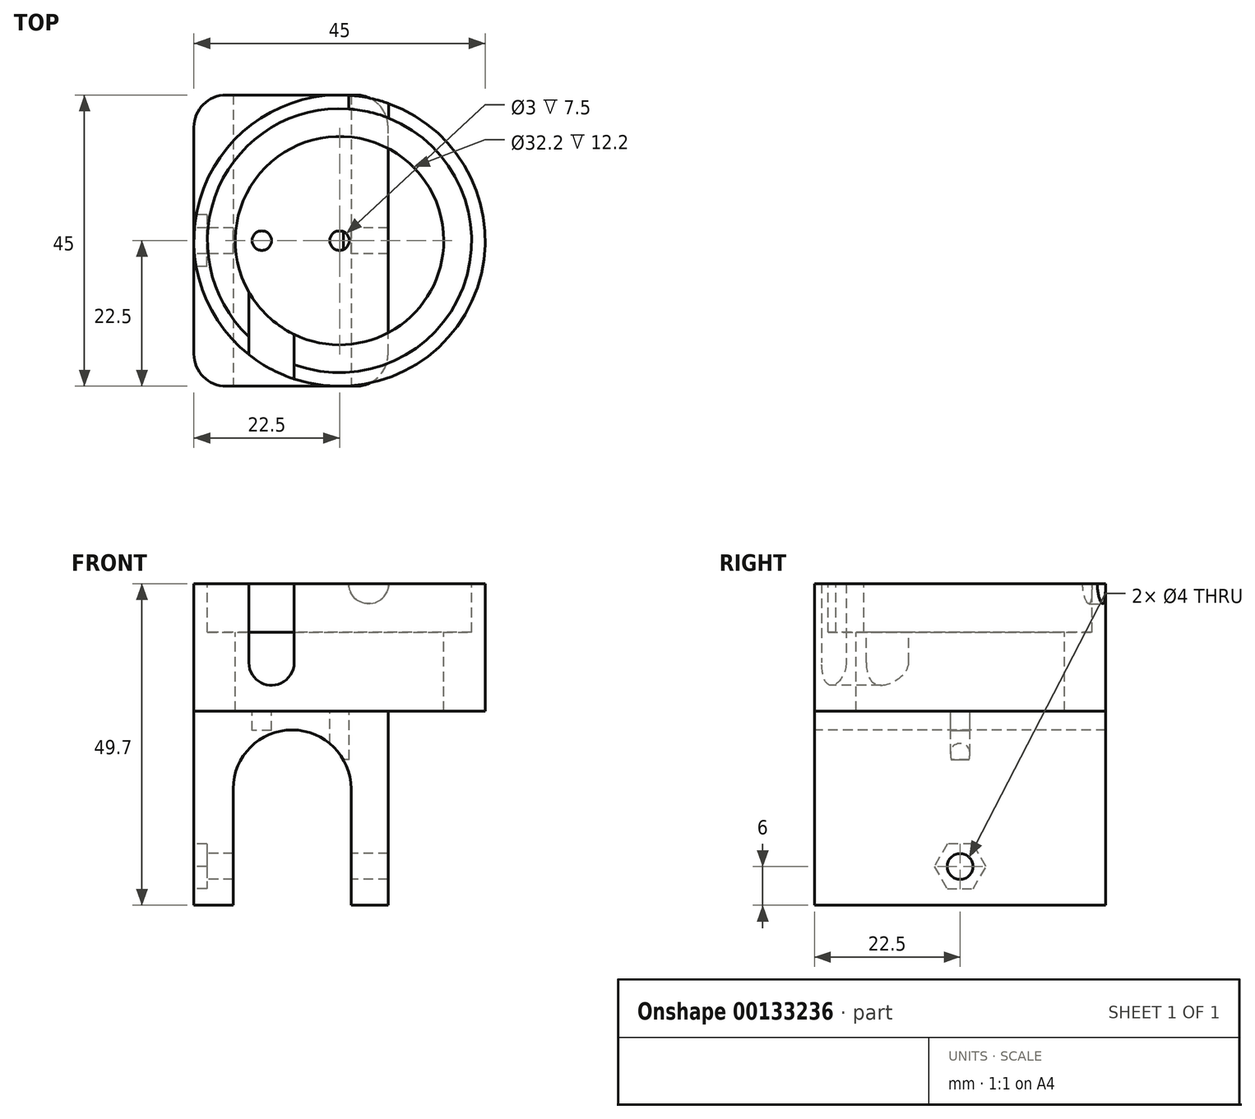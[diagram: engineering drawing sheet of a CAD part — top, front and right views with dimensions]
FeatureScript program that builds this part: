
annotation { "Feature Type Name" : "Feature", "Feature Type Description" : "" }
export const myFeature = defineFeature(function(context is Context, id is Id, definition is map)
    precondition{}
    {
        {
            var Q0;
            Q0=qCreatedBy(makeId("Top.planeOp"),FACE);
            var sketch = newSketch(context, id + "F0", { "sketchPlane" : qUnion([Q0])});
            skLineSegment(sketch, "E0.bottom", {"start": v(22.5, -22.5) * mm, "end": v(-22.5, -22.5) * mm});
            skLineSegment(sketch, "E0.top", {"start": v(22.5, 22.5) * mm, "end": v(-22.5, 22.5) * mm});
            skLineSegment(sketch, "E0.left", {"start": v(22.5, -22.5) * mm, "end": v(22.5, 22.5) * mm});
            skLineSegment(sketch, "E0.right", {"start": v(-22.5, -22.5) * mm, "end": v(-22.5, 22.5) * mm});
            skPoint(sketch, "E0.middle", {"position": v(0, 0) * mm});
            skSolve(sketch);
        }
        {
            var Q0;
            Q0 = qSketchRegion(id + "F0", true);
            extrude(context, id + "F1", {"entities" : qUnion([Q0]), "depth" : 19.7 * mm});
        }
        {
            var Q0;
            Q0=makeQuery(id+"F1.opExtrude","CAP_FACE",FACE,{"disambiguationData":[OSD([sQuery(id+"F0.wireOp",EDGE,"E0.bottom"),sQuery(id+"F0.wireOp",EDGE,"E0.top"),sQuery(id+"F0.wireOp",EDGE,"E0.left"),sQuery(id+"F0.wireOp",EDGE,"E0.right")])],"isStart":false});
            var sketch = newSketch(context, id + "F2", { "sketchPlane" : qUnion([Q0])});
            skCircle(sketch, "E1", {"center": v(0, 0) * mm, "radius": 20.4 * mm});
            skSolve(sketch);
        }
        {
            var Q0;
            Q0=makeQuery(id+"F2.imprint","IMPRINT",FACE,{"disambiguationData":[TD([[makeQuery(id+"F2.imprint","IMPRINT",EDGE,{"derivedFrom":sQuery(id+"F2.wireOp",EDGE,"E1")}),1.0]])]});
            extrude(context, id + "F3", {"entities" : qUnion([Q0]), "operationType" : NewBodyOperationType.REMOVE, "oppositeDirection" : true, "depth" : 7.5 * mm});
        }
        {
            var Q0;
            Q0=makeQuery(id+"F3.boolean.opBoolean","COPY",FACE,{"derivedFrom":makeQuery(id+"F3.opExtrude","CAP_FACE",FACE,{"disambiguationData":[OSD([sQuery(id+"F2.wireOp",EDGE,"E1")])],"isStart":false})});
            var sketch = newSketch(context, id + "F4", { "sketchPlane" : qUnion([Q0])});
            skCircle(sketch, "E2", {"center": v(0, 0) * mm, "radius": 16.1 * mm});
            skSolve(sketch);
        }
        {
            var Q0;
            Q0=makeQuery(id+"F4.imprint","IMPRINT",FACE,{"disambiguationData":[TD([[makeQuery(id+"F4.imprint","IMPRINT",EDGE,{"derivedFrom":sQuery(id+"F4.wireOp",EDGE,"E2")}),1.0]])]});
            extrude(context, id + "F5", {"entities" : qUnion([Q0]), "operationType" : NewBodyOperationType.REMOVE, "endBound" : BoundingType.UP_TO_NEXT, "oppositeDirection" : true, "depth" : 25 * mm});
        }
        {
            var Q0;
            Q0=makeQuery(id+"F1.opExtrude","SWEPT_FACE",FACE,{"disambiguationData":[OSD([sQuery(id+"F0.wireOp",EDGE,"E0.bottom")])]});
            var sketch = newSketch(context, id + "F6", { "sketchPlane" : qUnion([Q0])});
            skArc(sketch, "E3", {"start": v(-14, 7.5) * mm, "mid": v(-10.5, 4) * mm, "end": v(-7, 7.5) * mm});
            skLineSegment(sketch, "E4", {"start": v(-10.5, 7.5) * mm, "end": v(-22.5, 7.5) * mm, "construction": true});
            skLineSegment(sketch, "E5", {"start": v(-10.5, 7.5) * mm, "end": v(0, 7.5) * mm, "construction": true});
            skLineSegment(sketch, "E6", {"start": v(-7, 7.5) * mm, "end": v(-7, 19.7) * mm});
            skLineSegment(sketch, "E7", {"start": v(-14, 7.5) * mm, "end": v(-14, 19.7) * mm});
            skLineSegment(sketch, "E8", {"start": v(-7, 19.7) * mm, "end": v(-14, 19.7) * mm});
            skSolve(sketch);
        }
        {
            var Q0;
            Q0=makeQuery(id+"F6.imprint","IMPRINT",FACE,{"disambiguationData":[TD([[makeQuery(id+"F6.imprint","IMPRINT",EDGE,{"derivedFrom":sQuery(id+"F6.wireOp",EDGE,"E3")}),1.0]])]});
            extrude(context, id + "F7", {"entities" : qUnion([Q0]), "operationType" : NewBodyOperationType.REMOVE, "endBound" : BoundingType.UP_TO_NEXT, "oppositeDirection" : true, "depth" : 25 * mm});
        }
        {
            var Q0;
            Q0=makeQuery(id+"F1.opExtrude","SWEPT_FACE",FACE,{"disambiguationData":[OSD([sQuery(id+"F0.wireOp",EDGE,"E0.top")])]});
            var sketch = newSketch(context, id + "F8", { "sketchPlane" : qUnion([Q0])});
            skArc(sketch, "E9", {"start": v(-7.6, 19.7) * mm, "mid": v(-4.5, 16.6) * mm, "end": v(-1.4, 19.7) * mm});
            skLineSegment(sketch, "E10", {"start": v(-7.6, 19.7) * mm, "end": v(-1.4, 19.7) * mm});
            skSolve(sketch);
        }
        {
            var Q0;
            Q0=makeQuery(id+"F8.imprint","IMPRINT",FACE,{"disambiguationData":[TD([[makeQuery(id+"F8.imprint","IMPRINT",EDGE,{"derivedFrom":sQuery(id+"F8.wireOp",EDGE,"E9")}),1.0]])]});
            extrude(context, id + "F9", {"entities" : qUnion([Q0]), "operationType" : NewBodyOperationType.REMOVE, "endBound" : BoundingType.UP_TO_NEXT, "oppositeDirection" : true, "depth" : 25 * mm});
        }
        {
            var Q0;
            Q0=makeQuery(id+"F1.opExtrude","CAP_FACE",FACE,{"disambiguationData":[OSD([sQuery(id+"F0.wireOp",EDGE,"E0.bottom"),sQuery(id+"F0.wireOp",EDGE,"E0.top"),sQuery(id+"F0.wireOp",EDGE,"E0.left"),sQuery(id+"F0.wireOp",EDGE,"E0.right")])],"isStart":true});
            var sketch = newSketch(context, id + "F10", { "sketchPlane" : qUnion([Q0])});
            skLineSegment(sketch, "E11.bottom", {"start": v(-22.5, 22.5) * mm, "end": v(7.5, 22.5) * mm});
            skLineSegment(sketch, "E11.top", {"start": v(-22.5, -22.5) * mm, "end": v(7.5, -22.5) * mm});
            skLineSegment(sketch, "E11.left", {"start": v(-22.5, 22.5) * mm, "end": v(-22.5, -22.5) * mm});
            skLineSegment(sketch, "E11.right", {"start": v(7.5, 22.5) * mm, "end": v(7.5, -22.5) * mm});
            skSolve(sketch);
        }
        {
            var Q0;
            {var subQ1=sQuery(id+"F10.wireOp",EDGE,"E11.bottom");Q0=makeQuery(id+"F10.imprint","IMPRINT",FACE,{"disambiguationData":[TD([[makeQuery(id+"F10.imprint","IMPRINT",EDGE,{"derivedFrom":subQ1}),1.0]])]});}
            var Q1;
            {var subQ0=sQuery(id+"F10.wireOp",EDGE,"E11.right");var subQ1=makeQuery(id+"F5.boolean.opBoolean","COPY",EDGE,{"derivedFrom":makeQuery(id+"F5.opExtrude","TWEAK_EDGE",EDGE,{"derivedFrom":[makeQuery(id+"F1.opExtrude","CAP_FACE",FACE,{"disambiguationData":[OSD([sQuery(id+"F0.wireOp",EDGE,"E0.bottom"),sQuery(id+"F0.wireOp",EDGE,"E0.top"),sQuery(id+"F0.wireOp",EDGE,"E0.left"),sQuery(id+"F0.wireOp",EDGE,"E0.right")])],"isStart":true}),makeQuery(id+"F4.imprint","IMPRINT",EDGE,{"derivedFrom":sQuery(id+"F4.wireOp",EDGE,"E2")})]})});var subQ2=makeQuery(id+"F10.imprint","INTERSECT",VERTEX,{"disambiguationData":[OD(0.0)],"derivedFrom":[subQ1,subQ0]});Q1=makeQuery(id+"F10.imprint","IMPRINT",FACE,{"disambiguationData":[TD([[makeQuery(id+"F10.imprint","IMPRINT",EDGE,{"disambiguationData":[TD([[subQ2,-1.0]])],"derivedFrom":subQ0}),-1.0]])]});}
            extrude(context, id + "F11", {"entities" : qUnion([Q0, Q1]), "depth" : 30 * mm});
        }
        {
            var Q0;
            Q0=makeQuery(id+"F11.boolean.opBoolean","MERGE",FACE,{"derivedFrom":[makeQuery(id+"F1.opExtrude","SWEPT_FACE",FACE,{"disambiguationData":[OSD([sQuery(id+"F0.wireOp",EDGE,"E0.bottom")])]}),makeQuery(id+"F11.opExtrude","SWEPT_FACE",FACE,{"disambiguationData":[OSD([sQuery(id+"F10.wireOp",EDGE,"E11.bottom")])]})]});
            var sketch = newSketch(context, id + "F12", { "sketchPlane" : qUnion([Q0])});
            skLineSegment(sketch, "E12", {"start": v(-7.5, -30) * mm, "end": v(-7, 19.7) * mm, "construction": true});
            skArc(sketch, "E13", {"start": v(1.78, -12) * mm, "mid": v(-7.32, -2.9) * mm, "end": v(-16.42, -12) * mm});
            skLineSegment(sketch, "E14", {"start": v(-22.5, -12) * mm, "end": v(7.5, -12) * mm, "construction": true});
            skLineSegment(sketch, "E15", {"start": v(-16.42, -12) * mm, "end": v(-16.42, -30) * mm});
            skLineSegment(sketch, "E16", {"start": v(1.78, -12) * mm, "end": v(1.78, -30) * mm});
            skLineSegment(sketch, "E17", {"start": v(1.78, -30) * mm, "end": v(-16.42, -30) * mm});
            skSolve(sketch);
        }
        {
            var Q0;
            Q0=makeQuery(id+"F12.imprint","IMPRINT",FACE,{"disambiguationData":[TD([[makeQuery(id+"F12.imprint","IMPRINT",EDGE,{"derivedFrom":sQuery(id+"F12.wireOp",EDGE,"E13")}),1.0]])]});
            extrude(context, id + "F13", {"entities" : qUnion([Q0]), "operationType" : NewBodyOperationType.REMOVE, "endBound" : BoundingType.UP_TO_NEXT, "oppositeDirection" : true, "depth" : 25 * mm});
        }
        {
            var Q0;
            Q0=makeQuery(id+"F1.opExtrude","SWEPT_EDGE",EDGE,{"disambiguationData":[OSD([sQuery(id+"F0.wireOp",EDGE,"E0.bottom"),sQuery(id+"F0.wireOp",EDGE,"E0.left")])]});
            var Q1;
            Q1=makeQuery(id+"F1.opExtrude","SWEPT_EDGE",EDGE,{"disambiguationData":[OSD([sQuery(id+"F0.wireOp",EDGE,"E0.bottom"),sQuery(id+"F0.wireOp",EDGE,"E0.right")])]});
            var Q2;
            Q2=makeQuery(id+"F1.opExtrude","SWEPT_EDGE",EDGE,{"disambiguationData":[OSD([sQuery(id+"F0.wireOp",EDGE,"E0.top"),sQuery(id+"F0.wireOp",EDGE,"E0.right")])]});
            var Q3;
            Q3=makeQuery(id+"F1.opExtrude","SWEPT_EDGE",EDGE,{"disambiguationData":[OSD([sQuery(id+"F0.wireOp",EDGE,"E0.top"),sQuery(id+"F0.wireOp",EDGE,"E0.left")])]});
            fillet(context, id + "F14", {"entities" : qUnion([Q0, Q1, Q2, Q3]), "radius" : 22.5 * mm, "tangentPropagation" : true, "allowEdgeOverflow" : false});
        }
        {
            var Q0;
            Q0=makeQuery(id+"F11.opExtrude","SWEPT_FACE",FACE,{"disambiguationData":[OSD([sQuery(id+"F10.wireOp",EDGE,"E11.left")])]});
            var sketch = newSketch(context, id + "F15", { "sketchPlane" : qUnion([Q0])});
            skCircle(sketch, "E18.cCircle", {"center": v(0, -24) * mm, "radius": 4 * mm, "construction": true});
            skLineSegment(sketch, "E18.0", {"start": v(2, -27.46) * mm, "end": v(-2, -27.46) * mm});
            skLineSegment(sketch, "E18.1", {"start": v(-2, -27.46) * mm, "end": v(-4, -24) * mm});
            skLineSegment(sketch, "E18.2", {"start": v(-4, -24) * mm, "end": v(-2, -20.54) * mm});
            skLineSegment(sketch, "E18.3", {"start": v(-2, -20.54) * mm, "end": v(2, -20.54) * mm});
            skLineSegment(sketch, "E18.4", {"start": v(2, -20.54) * mm, "end": v(4, -24) * mm});
            skLineSegment(sketch, "E18.5", {"start": v(4, -24) * mm, "end": v(2, -27.46) * mm});
            skSolve(sketch);
        }
        {
            var Q0;
            Q0=makeQuery(id+"F15.imprint","IMPRINT",FACE,{"disambiguationData":[TD([[makeQuery(id+"F15.imprint","IMPRINT",EDGE,{"derivedFrom":sQuery(id+"F15.wireOp",EDGE,"E18.0")}),-1.0]])]});
            extrude(context, id + "F16", {"entities" : qUnion([Q0]), "operationType" : NewBodyOperationType.REMOVE, "oppositeDirection" : true, "depth" : 2 * mm});
        }
        {
            var Q0;
            Q0=makeQuery(id+"F16.boolean.opBoolean","COPY",FACE,{"derivedFrom":makeQuery(id+"F16.opExtrude","CAP_FACE",FACE,{"disambiguationData":[OSD([sQuery(id+"F15.wireOp",EDGE,"E18.0"),sQuery(id+"F15.wireOp",EDGE,"E18.1"),sQuery(id+"F15.wireOp",EDGE,"E18.2"),sQuery(id+"F15.wireOp",EDGE,"E18.3"),sQuery(id+"F15.wireOp",EDGE,"E18.4"),sQuery(id+"F15.wireOp",EDGE,"E18.5")])],"isStart":false})});
            var sketch = newSketch(context, id + "F17", { "sketchPlane" : qUnion([Q0])});
            skLineSegment(sketch, "E19", {"start": v(-4, -24) * mm, "end": v(4, -24) * mm, "construction": true});
            skCircle(sketch, "E20", {"center": v(0, -24) * mm, "radius": 2 * mm});
            skSolve(sketch);
        }
        {
            var Q0;
            Q0=makeQuery(id+"F17.imprint","IMPRINT",FACE,{"disambiguationData":[TD([[makeQuery(id+"F17.imprint","IMPRINT",EDGE,{"derivedFrom":sQuery(id+"F17.wireOp",EDGE,"E20")}),1.0]])]});
            extrude(context, id + "F18", {"entities" : qUnion([Q0]), "operationType" : NewBodyOperationType.REMOVE, "endBound" : BoundingType.THROUGH_ALL, "oppositeDirection" : true, "depth" : 25 * mm});
        }
        {
            var Q0;
            Q0=makeQuery(id+"F11.opExtrude","SWEPT_EDGE",EDGE,{"disambiguationData":[OSD([sQuery(id+"F10.wireOp",EDGE,"E11.bottom"),sQuery(id+"F10.wireOp",EDGE,"E11.left")])]});
            var Q1;
            Q1=makeQuery(id+"F11.opExtrude","SWEPT_EDGE",EDGE,{"disambiguationData":[OSD([sQuery(id+"F0.wireOp",EDGE,"E0.bottom"),sQuery(id+"F10.wireOp",EDGE,"E11.bottom"),sQuery(id+"F10.wireOp",EDGE,"E11.right")])]});
            var Q2;
            Q2=makeQuery(id+"F11.opExtrude","SWEPT_EDGE",EDGE,{"disambiguationData":[OSD([sQuery(id+"F0.wireOp",EDGE,"E0.top"),sQuery(id+"F10.wireOp",EDGE,"E11.top"),sQuery(id+"F10.wireOp",EDGE,"E11.right")])]});
            var Q3;
            Q3=makeQuery(id+"F11.opExtrude","SWEPT_EDGE",EDGE,{"disambiguationData":[OSD([sQuery(id+"F10.wireOp",EDGE,"E11.top"),sQuery(id+"F10.wireOp",EDGE,"E11.left")])]});
            fillet(context, id + "F19", {"entities" : qUnion([Q0, Q1, Q2, Q3]), "radius" : 5 * mm, "tangentPropagation" : true, "allowEdgeOverflow" : false});
        }
        {
            var Q0;
            Q0=makeQuery(id+"F11.opExtrude","CAP_FACE",FACE,{"disambiguationData":[OSD([sQuery(id+"F10.wireOp",EDGE,"E11.bottom"),sQuery(id+"F10.wireOp",EDGE,"E11.top"),sQuery(id+"F10.wireOp",EDGE,"E11.left"),sQuery(id+"F10.wireOp",EDGE,"E11.right")])],"isStart":true});
            var sketch = newSketch(context, id + "F20", { "sketchPlane" : qUnion([Q0])});
            skCircle(sketch, "E21", {"center": v(0, 0) * mm, "radius": 1.5 * mm});
            skSolve(sketch);
        }
        {
            var Q0;
            Q0=makeQuery(id+"F20.imprint","IMPRINT",FACE,{"disambiguationData":[TD([[makeQuery(id+"F20.imprint","IMPRINT",EDGE,{"derivedFrom":sQuery(id+"F20.wireOp",EDGE,"E21")}),1.0]])]});
            var Q1;
            Q1=sQuery(id+"F20.wireOp",EDGE,"E21");
            extrude(context, id + "F21", {"entities" : qUnion([Q0]), "operationType" : NewBodyOperationType.REMOVE, "surfaceEntities" : qUnion([Q1]), "oppositeDirection" : true, "depth" : 7.5 * mm});
        }
        {
            var Q0;
            Q0=makeQuery(id+"F11.opExtrude","CAP_FACE",FACE,{"disambiguationData":[OSD([sQuery(id+"F10.wireOp",EDGE,"E11.bottom"),sQuery(id+"F10.wireOp",EDGE,"E11.top"),sQuery(id+"F10.wireOp",EDGE,"E11.left"),sQuery(id+"F10.wireOp",EDGE,"E11.right")])],"isStart":true});
            var sketch = newSketch(context, id + "F22", { "sketchPlane" : qUnion([Q0])});
            skLineSegment(sketch, "E22", {"start": v(7.5, 0) * mm, "end": v(-22.5, 0) * mm, "construction": true});
            skCircle(sketch, "E23", {"center": v(-12, 0) * mm, "radius": 1.5 * mm});
            skSolve(sketch);
        }
        {
            var Q0;
            Q0=makeQuery(id+"F22.imprint","IMPRINT",FACE,{"disambiguationData":[TD([[makeQuery(id+"F22.imprint","IMPRINT",EDGE,{"derivedFrom":sQuery(id+"F22.wireOp",EDGE,"E23")}),1.0]])]});
            var Q1;
            Q1=sQuery(id+"F22.wireOp",EDGE,"E23");
            extrude(context, id + "F23", {"entities" : qUnion([Q0]), "operationType" : NewBodyOperationType.REMOVE, "surfaceEntities" : qUnion([Q1]), "oppositeDirection" : true, "depth" : 3 * mm});
        }
    });
